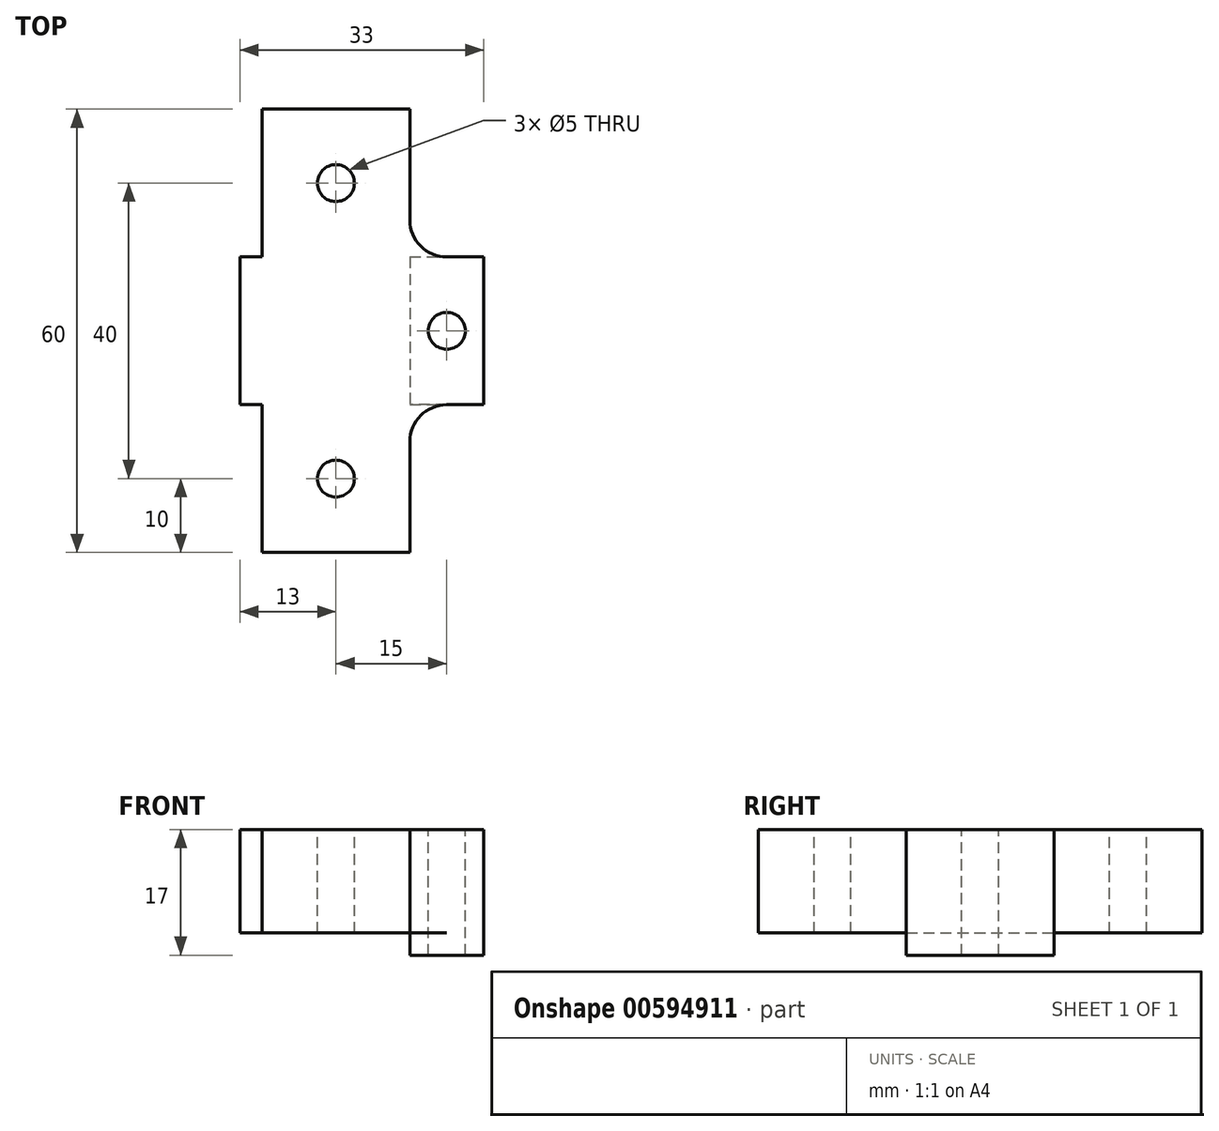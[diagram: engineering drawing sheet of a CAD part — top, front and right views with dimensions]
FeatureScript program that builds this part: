
annotation { "Feature Type Name" : "Feature", "Feature Type Description" : "" }
export const myFeature = defineFeature(function(context is Context, id is Id, definition is map)
    precondition{}
    {
        {
            var Q0;
            Q0=qCreatedBy(makeId("Top.planeOp"),FACE);
            var sketch = newSketch(context, id + "F0", { "sketchPlane" : qUnion([Q0])});
            skLineSegment(sketch, "E0.bottom", {"start": v(0, 0) * mm, "end": v(20, 0) * mm});
            skLineSegment(sketch, "E0.top", {"start": v(0, 60) * mm, "end": v(20, 60) * mm});
            skLineSegment(sketch, "E0.left", {"start": v(0, 0) * mm, "end": v(0, 60) * mm});
            skLineSegment(sketch, "E0.right", {"start": v(20, 0) * mm, "end": v(20, 60) * mm});
            skLineSegment(sketch, "E1.bottom", {"start": v(7.5, 52.5) * mm, "end": v(12.5, 52.5) * mm});
            skLineSegment(sketch, "E1.top", {"start": v(7.5, 47.5) * mm, "end": v(12.5, 47.5) * mm});
            skLineSegment(sketch, "E1.left", {"start": v(7.5, 52.5) * mm, "end": v(7.5, 47.5) * mm});
            skLineSegment(sketch, "E1.right", {"start": v(12.5, 52.5) * mm, "end": v(12.5, 47.5) * mm});
            skLineSegment(sketch, "E2.bottom", {"start": v(7.5, 7.5) * mm, "end": v(12.5, 7.5) * mm});
            skLineSegment(sketch, "E2.top", {"start": v(7.5, 12.5) * mm, "end": v(12.5, 12.5) * mm});
            skLineSegment(sketch, "E2.left", {"start": v(7.5, 7.5) * mm, "end": v(7.5, 12.5) * mm});
            skLineSegment(sketch, "E2.right", {"start": v(12.5, 7.5) * mm, "end": v(12.5, 12.5) * mm});
            skLineSegment(sketch, "E3.bottom", {"start": v(20, 20) * mm, "end": v(30, 20) * mm});
            skLineSegment(sketch, "E3.top", {"start": v(20, 40) * mm, "end": v(30, 40) * mm});
            skLineSegment(sketch, "E3.left", {"start": v(20, 20) * mm, "end": v(20, 40) * mm});
            skLineSegment(sketch, "E3.right", {"start": v(30, 20) * mm, "end": v(30, 40) * mm});
            skLineSegment(sketch, "E4.bottom", {"start": v(0, 20) * mm, "end": v(-3, 20) * mm});
            skLineSegment(sketch, "E4.top", {"start": v(0, 40) * mm, "end": v(-3, 40) * mm});
            skLineSegment(sketch, "E4.left", {"start": v(0, 20) * mm, "end": v(0, 40) * mm});
            skLineSegment(sketch, "E4.right", {"start": v(-3, 20) * mm, "end": v(-3, 40) * mm});
            skSolve(sketch);
        }
        {
            var Q0;
            Q0 = qSketchRegion(id + "F0", true);
            extrude(context, id + "F1", {"entities" : qUnion([Q0]), "depth" : 14 * mm, "offsetDistance" : 25 * mm});
        }
        {
            var Q0;
            Q0=makeQuery(id+"F1.opExtrude","CAP_FACE",FACE,{"disambiguationData":[OSD([sQuery(id+"F0.wireOp",EDGE,"E0.bottom"),sQuery(id+"F0.wireOp",EDGE,"E0.top"),sQuery(id+"F0.wireOp",EDGE,"E0.left"),sQuery(id+"F0.wireOp",EDGE,"E0.right"),sQuery(id+"F0.wireOp",EDGE,"E1.bottom"),sQuery(id+"F0.wireOp",EDGE,"E1.top"),sQuery(id+"F0.wireOp",EDGE,"E1.left"),sQuery(id+"F0.wireOp",EDGE,"E1.right"),sQuery(id+"F0.wireOp",EDGE,"E2.bottom"),sQuery(id+"F0.wireOp",EDGE,"E2.top"),sQuery(id+"F0.wireOp",EDGE,"E2.left"),sQuery(id+"F0.wireOp",EDGE,"E2.right"),sQuery(id+"F0.wireOp",EDGE,"E3.bottom"),sQuery(id+"F0.wireOp",EDGE,"E3.top"),sQuery(id+"F0.wireOp",EDGE,"E3.right"),sQuery(id+"F0.wireOp",EDGE,"E4.bottom"),sQuery(id+"F0.wireOp",EDGE,"E4.top"),sQuery(id+"F0.wireOp",EDGE,"E4.right")])],"isStart":true});
            var sketch = newSketch(context, id + "F2", { "sketchPlane" : qUnion([Q0])});
            skLineSegment(sketch, "E5.bottom", {"start": v(20, -40) * mm, "end": v(30, -40) * mm});
            skLineSegment(sketch, "E5.top", {"start": v(20, -20) * mm, "end": v(30, -20) * mm});
            skLineSegment(sketch, "E5.left", {"start": v(20, -40) * mm, "end": v(20, -20) * mm});
            skLineSegment(sketch, "E5.right", {"start": v(30, -40) * mm, "end": v(30, -20) * mm});
            skSolve(sketch);
        }
        {
            var Q0;
            Q0 = qSketchRegion(id + "F2", true);
            extrude(context, id + "F3", {"entities" : qUnion([Q0]), "operationType" : NewBodyOperationType.ADD, "depth" : 3 * mm, "offsetDistance" : 25 * mm});
        }
        {
            var Q0;
            Q0=makeQuery(id+"F1.opExtrude","SWEPT_EDGE",EDGE,{"disambiguationData":[OSD([sQuery(id+"F0.wireOp",EDGE,"E0.right"),sQuery(id+"F0.wireOp",EDGE,"E3.top"),sQuery(id+"F0.wireOp",EDGE,"E3.left")])]});
            fillet(context, id + "F4", {"entities" : qUnion([Q0]), "radius" : 5 * mm, "tangentPropagation" : true, "allowEdgeOverflow" : false});
        }
        {
            var Q0;
            Q0=makeQuery(id+"F1.opExtrude","SWEPT_EDGE",EDGE,{"disambiguationData":[OSD([sQuery(id+"F0.wireOp",EDGE,"E0.right"),sQuery(id+"F0.wireOp",EDGE,"E3.bottom"),sQuery(id+"F0.wireOp",EDGE,"E3.left")])]});
            fillet(context, id + "F5", {"entities" : qUnion([Q0]), "radius" : 5 * mm, "tangentPropagation" : true, "allowEdgeOverflow" : false});
        }
        {
            var Q0;
            Q0=makeQuery(id+"F1.opExtrude","SWEPT_EDGE",EDGE,{"disambiguationData":[OSD([sQuery(id+"F0.wireOp",EDGE,"E2.bottom"),sQuery(id+"F0.wireOp",EDGE,"E2.left")])]});
            var Q1;
            Q1=makeQuery(id+"F1.opExtrude","SWEPT_EDGE",EDGE,{"disambiguationData":[OSD([sQuery(id+"F0.wireOp",EDGE,"E2.top"),sQuery(id+"F0.wireOp",EDGE,"E2.left")])]});
            var Q2;
            Q2=makeQuery(id+"F1.opExtrude","SWEPT_EDGE",EDGE,{"disambiguationData":[OSD([sQuery(id+"F0.wireOp",EDGE,"E2.top"),sQuery(id+"F0.wireOp",EDGE,"E2.right")])]});
            var Q3;
            Q3=makeQuery(id+"F1.opExtrude","SWEPT_EDGE",EDGE,{"disambiguationData":[OSD([sQuery(id+"F0.wireOp",EDGE,"E2.bottom"),sQuery(id+"F0.wireOp",EDGE,"E2.right")])]});
            fillet(context, id + "F6", {"entities" : qUnion([Q0, Q1, Q2, Q3]), "radius" : 2.5 * mm, "tangentPropagation" : true, "allowEdgeOverflow" : false});
        }
        {
            var Q0;
            Q0=makeQuery(id+"F1.opExtrude","SWEPT_EDGE",EDGE,{"disambiguationData":[OSD([sQuery(id+"F0.wireOp",EDGE,"E1.top"),sQuery(id+"F0.wireOp",EDGE,"E1.right")])]});
            var Q1;
            Q1=makeQuery(id+"F1.opExtrude","SWEPT_EDGE",EDGE,{"disambiguationData":[OSD([sQuery(id+"F0.wireOp",EDGE,"E1.top"),sQuery(id+"F0.wireOp",EDGE,"E1.left")])]});
            var Q2;
            Q2=makeQuery(id+"F1.opExtrude","SWEPT_EDGE",EDGE,{"disambiguationData":[OSD([sQuery(id+"F0.wireOp",EDGE,"E1.bottom"),sQuery(id+"F0.wireOp",EDGE,"E1.left")])]});
            var Q3;
            Q3=makeQuery(id+"F1.opExtrude","SWEPT_EDGE",EDGE,{"disambiguationData":[OSD([sQuery(id+"F0.wireOp",EDGE,"E1.bottom"),sQuery(id+"F0.wireOp",EDGE,"E1.right")])]});
            fillet(context, id + "F7", {"entities" : qUnion([Q0, Q1, Q2, Q3]), "radius" : 2.5 * mm, "tangentPropagation" : true, "allowEdgeOverflow" : false});
        }
        {
            var Q0;
            Q0=makeQuery(id+"F1.opExtrude","CAP_FACE",FACE,{"disambiguationData":[OSD([sQuery(id+"F0.wireOp",EDGE,"E0.bottom"),sQuery(id+"F0.wireOp",EDGE,"E0.top"),sQuery(id+"F0.wireOp",EDGE,"E0.left"),sQuery(id+"F0.wireOp",EDGE,"E0.right"),sQuery(id+"F0.wireOp",EDGE,"E1.bottom"),sQuery(id+"F0.wireOp",EDGE,"E1.top"),sQuery(id+"F0.wireOp",EDGE,"E1.left"),sQuery(id+"F0.wireOp",EDGE,"E1.right"),sQuery(id+"F0.wireOp",EDGE,"E2.bottom"),sQuery(id+"F0.wireOp",EDGE,"E2.top"),sQuery(id+"F0.wireOp",EDGE,"E2.left"),sQuery(id+"F0.wireOp",EDGE,"E2.right"),sQuery(id+"F0.wireOp",EDGE,"E3.bottom"),sQuery(id+"F0.wireOp",EDGE,"E3.top"),sQuery(id+"F0.wireOp",EDGE,"E3.right"),sQuery(id+"F0.wireOp",EDGE,"E4.bottom"),sQuery(id+"F0.wireOp",EDGE,"E4.top"),sQuery(id+"F0.wireOp",EDGE,"E4.right")])],"isStart":false});
            var sketch = newSketch(context, id + "F8", { "sketchPlane" : qUnion([Q0])});
            skCircle(sketch, "E6", {"center": v(25, 30) * mm, "radius": 2.5 * mm});
            skSolve(sketch);
        }
        {
            var Q0;
            Q0 = qSketchRegion(id + "F8", true);
            extrude(context, id + "F9", {"entities" : qUnion([Q0]), "operationType" : NewBodyOperationType.REMOVE, "oppositeDirection" : true, "depth" : 25 * mm, "offsetDistance" : 25 * mm});
        }
    });
